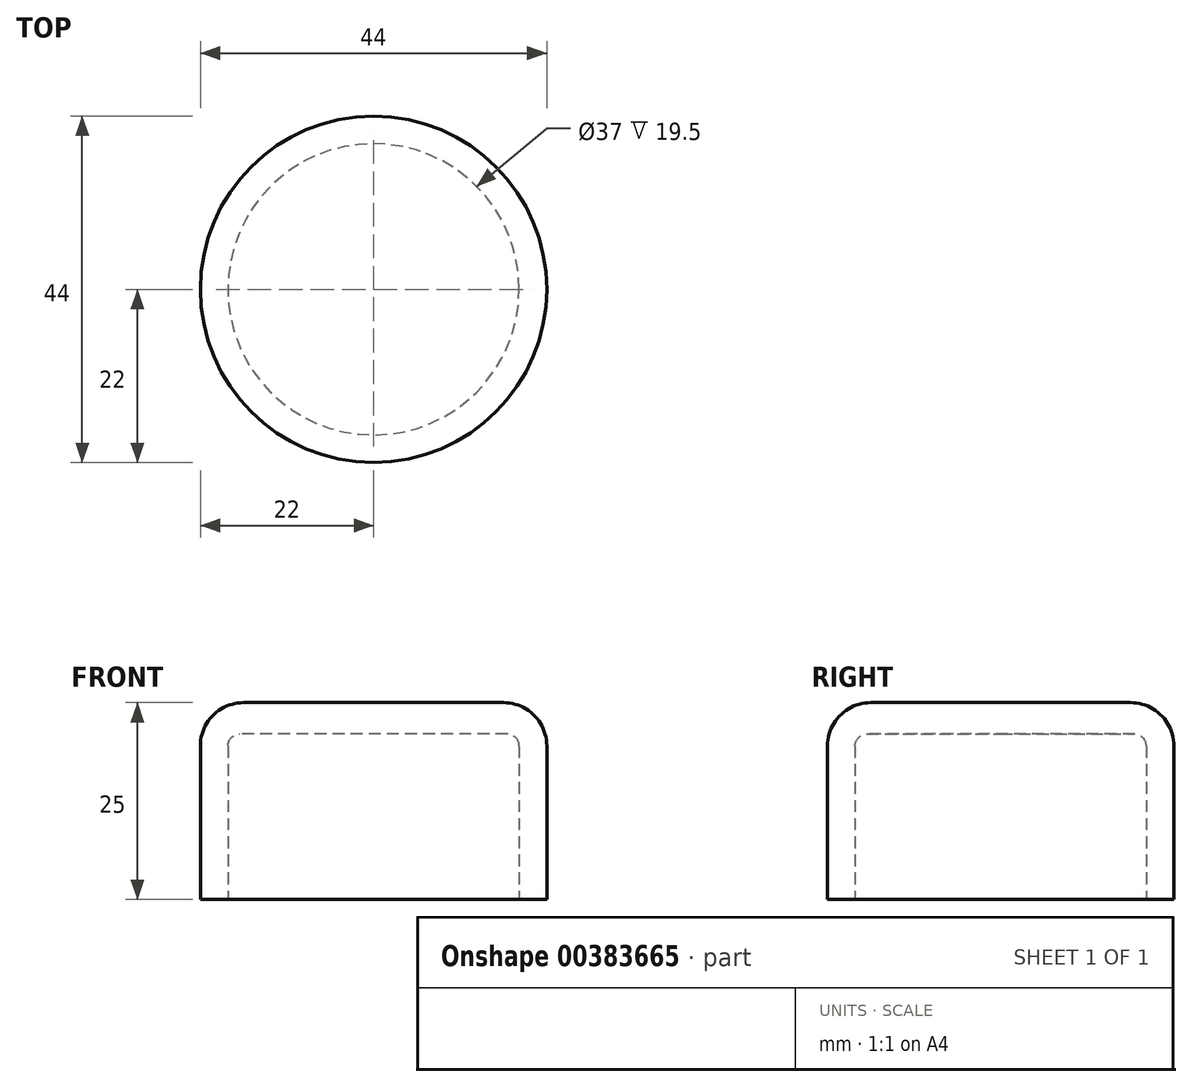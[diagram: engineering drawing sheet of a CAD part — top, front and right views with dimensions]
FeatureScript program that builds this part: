
annotation { "Feature Type Name" : "Feature", "Feature Type Description" : "" }
export const myFeature = defineFeature(function(context is Context, id is Id, definition is map)
    precondition{}
    {
        {
            var Q0;
            Q0=qCreatedBy(makeId("Top.planeOp"),FACE);
            var sketch = newSketch(context, id + "F0", { "sketchPlane" : qUnion([Q0])});
            skCircle(sketch, "E0", {"center": v(0, 0) * mm, "radius": 22 * mm});
            skSolve(sketch);
        }
        {
            var Q0;
            Q0 = qSketchRegion(id + "F0", true);
            extrude(context, id + "F1", {"entities" : qUnion([Q0]), "depth" : 25 * mm, "offsetDistance" : 25.4 * mm});
        }
        {
            var Q0;
            Q0=makeQuery(id+"F1.opExtrude","CAP_EDGE",EDGE,{"disambiguationData":[OSD([sQuery(id+"F0.wireOp",EDGE,"E0")])],"isStart":false});
            fillet(context, id + "F2", {"entities" : qUnion([Q0]), "radius" : 5.5 * mm, "tangentPropagation" : true, "allowEdgeOverflow" : false});
        }
        {
            var Q0;
            Q0=qCreatedBy(makeId("Top.planeOp"),FACE);
            var sketch = newSketch(context, id + "F3", { "sketchPlane" : qUnion([Q0])});
            skCircle(sketch, "E1", {"center": v(0, 0) * mm, "radius": 18.5 * mm});
            skSolve(sketch);
        }
        {
            var Q0;
            Q0 = qSketchRegion(id + "F3", true);
            extrude(context, id + "F4", {"entities" : qUnion([Q0]), "operationType" : NewBodyOperationType.REMOVE, "depth" : 21 * mm});
        }
        {
            var Q0;
            Q0=makeQuery(id+"F4.boolean.opBoolean","COPY",EDGE,{"derivedFrom":makeQuery(id+"F4.opExtrude","CAP_EDGE",EDGE,{"disambiguationData":[OSD([sQuery(id+"F3.wireOp",EDGE,"E1")])],"isStart":false})});
            fillet(context, id + "F5", {"entities" : qUnion([Q0]), "radius" : 1.5 * mm, "tangentPropagation" : true, "allowEdgeOverflow" : false});
        }
    });
